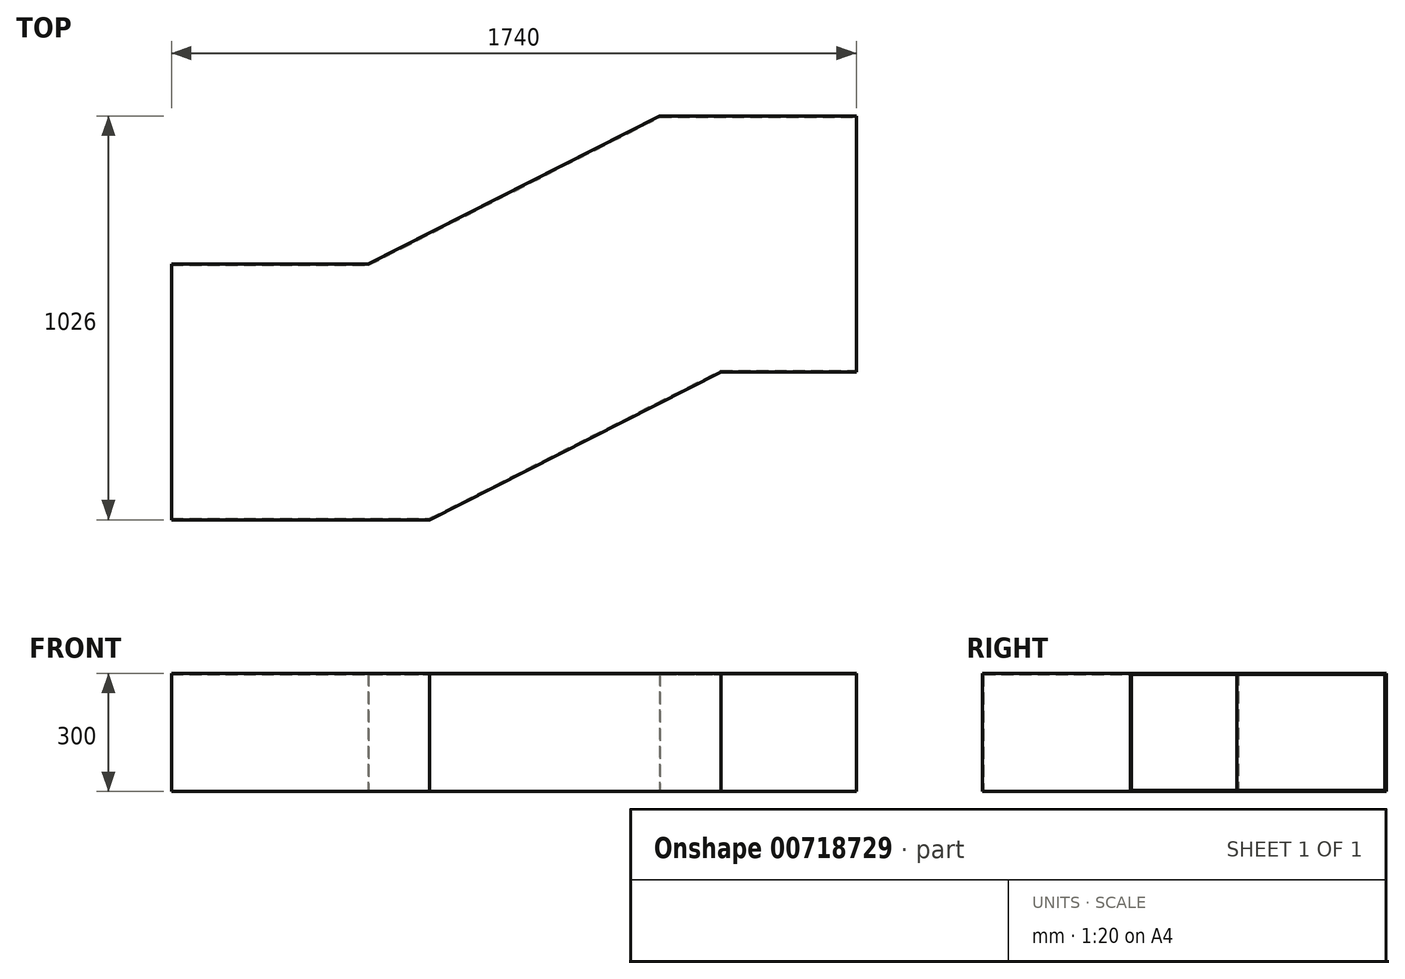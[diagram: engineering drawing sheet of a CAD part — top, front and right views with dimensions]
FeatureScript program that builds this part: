
annotation { "Feature Type Name" : "Feature", "Feature Type Description" : "" }
export const myFeature = defineFeature(function(context is Context, id is Id, definition is map)
    precondition{}
    {
        {
            var Q0;
            Q0=qCreatedBy(makeId("Top.planeOp"),FACE);
            var sketch = newSketch(context, id + "F0", { "sketchPlane" : qUnion([Q0])});
            skLineSegment(sketch, "E0.bottom", {"start": v(0, 0) * mm, "end": v(655.66, 0) * mm});
            skLineSegment(sketch, "E0.top", {"start": v(0, 650) * mm, "end": v(500, 650) * mm});
            skLineSegment(sketch, "E0.left", {"start": v(0, 0) * mm, "end": v(0, 650) * mm});
            skLineSegment(sketch, "E1.bottom", {"start": v(1395.66, 376) * mm, "end": v(1740, 376) * mm});
            skLineSegment(sketch, "E1.top", {"start": v(1240, 1026) * mm, "end": v(1740, 1026) * mm});
            skLineSegment(sketch, "E1.right", {"start": v(1740, 376) * mm, "end": v(1740, 1026) * mm});
            skLineSegment(sketch, "E2", {"start": v(500, 650) * mm, "end": v(1240, 1026) * mm});
            skLineSegment(sketch, "E3", {"start": v(655.66, 0) * mm, "end": v(1395.66, 376) * mm});
            skSolve(sketch);
        }
        {
            var Q0;
            Q0=makeQuery(id+"F0.imprint","IMPRINT",FACE,{"disambiguationData":[TD([[makeQuery(id+"F0.imprint","IMPRINT",EDGE,{"derivedFrom":sQuery(id+"F0.wireOp",EDGE,"E0.bottom")}),1.0]])]});
            extrude(context, id + "F1", {"entities" : qUnion([Q0]), "depth" : 300 * mm, "offsetDistance" : 25 * mm});
        }
        {
            var Q0;
            Q0=makeQuery(id+"F1.opExtrude","SWEPT_FACE",FACE,{"disambiguationData":[OSD([sQuery(id+"F0.wireOp",EDGE,"E0.left")])]});
            var Q1;
            Q1=makeQuery(id+"F1.opExtrude","SWEPT_FACE",FACE,{"disambiguationData":[OSD([sQuery(id+"F0.wireOp",EDGE,"E1.right")])]});
            shell(context, id + "F2", {"entities" : qUnion([Q0, Q1]), "thickness" : 3 * mm});
        }
    });
